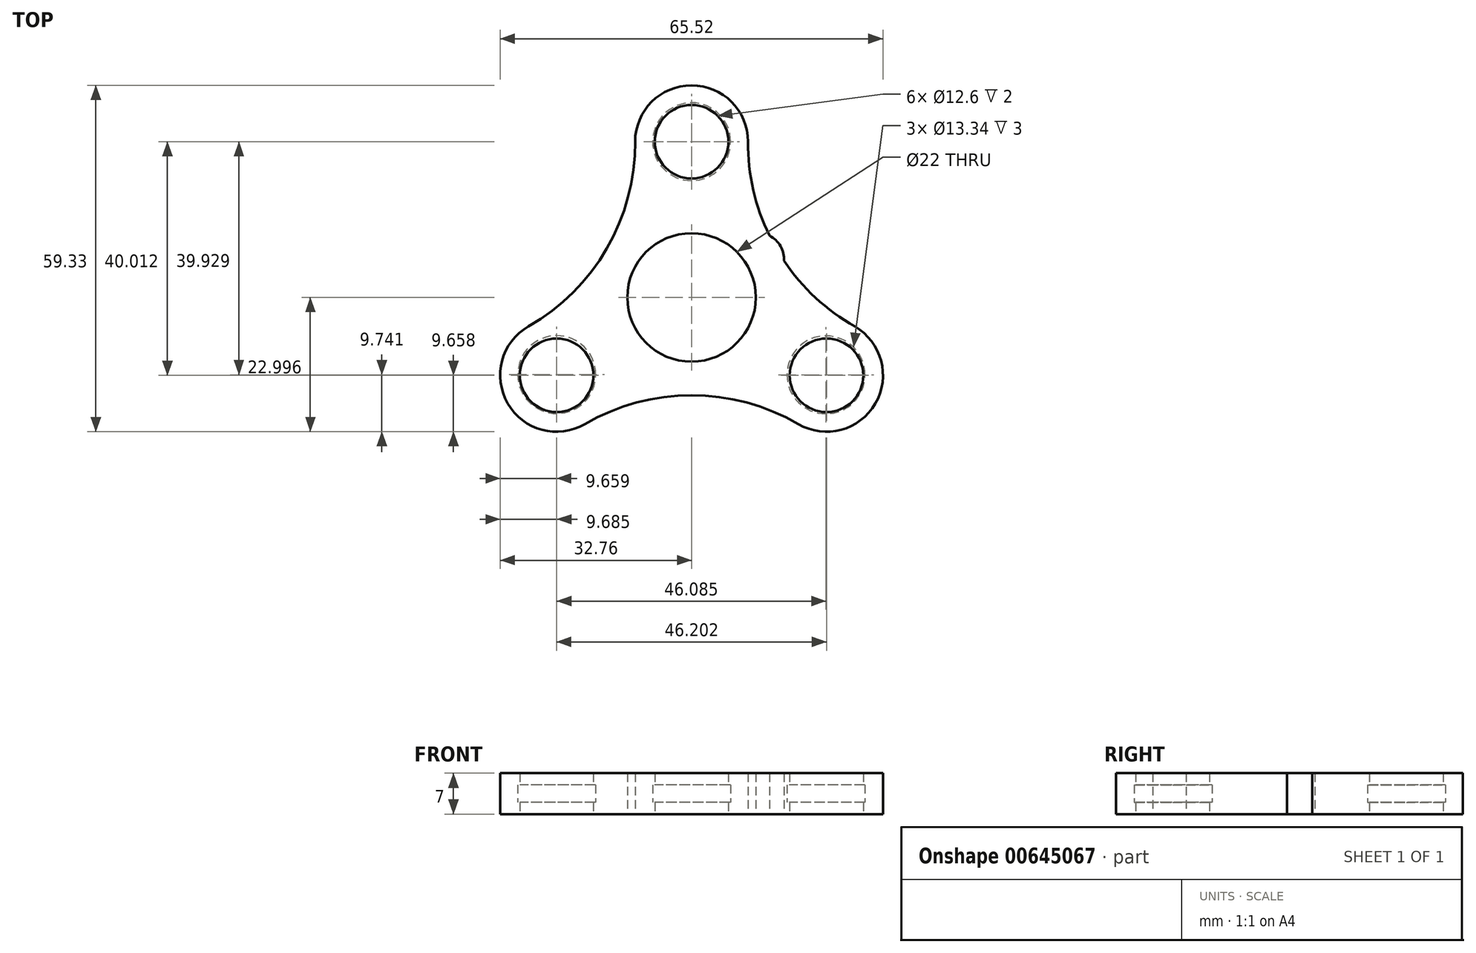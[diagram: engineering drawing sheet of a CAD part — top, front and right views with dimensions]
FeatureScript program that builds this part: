
annotation { "Feature Type Name" : "Feature", "Feature Type Description" : "" }
export const myFeature = defineFeature(function(context is Context, id is Id, definition is map)
    precondition{}
    {
        {
            var Q0;
            Q0=qCreatedBy(makeId("Top.planeOp"),FACE);
            var sketch = newSketch(context, id + "F0", { "sketchPlane" : qUnion([Q0])});
            skCircle(sketch, "E0", {"center": v(0, 0) * mm, "radius": 6.3 * mm});
            skCircle(sketch, "E1", {"center": v(0, 0) * mm, "radius": 9.66 * mm});
            skCircle(sketch, "E2.1.0", {"center": v(-23.1, -40.01) * mm, "radius": 9.66 * mm});
            skCircle(sketch, "E2.1.1", {"center": v(-23.1, -40.01) * mm, "radius": 6.3 * mm});
            skCircle(sketch, "E2.2.0", {"center": v(23.1, -40.01) * mm, "radius": 9.66 * mm});
            skCircle(sketch, "E2.2.1", {"center": v(23.1, -40.01) * mm, "radius": 6.3 * mm});
            skPoint(sketch, "E2.center", {"position": v(0, -26.67) * mm});
            skLineSegment(sketch, "E3", {"start": v(0, 0) * mm, "end": v(-9.66, 0) * mm, "construction": true});
            skCircle(sketch, "E4", {"center": v(0, -26.67) * mm, "radius": 11 * mm});
            skLineSegment(sketch, "E5", {"start": v(0, -26.67) * mm, "end": v(-23.1, -40.01) * mm, "construction": true});
            skLineSegment(sketch, "E6", {"start": v(23.1, -40.01) * mm, "end": v(0, -26.67) * mm, "construction": true});
            skLineSegment(sketch, "E7", {"start": v(0, -26.67) * mm, "end": v(0, 0) * mm, "construction": true});
            skLineSegment(sketch, "E8", {"start": v(23.1, -40.01) * mm, "end": v(27.93, -31.64) * mm, "construction": true});
            skLineSegment(sketch, "E9", {"start": v(0, 0) * mm, "end": v(9.66, 0) * mm, "construction": true});
            skLineSegment(sketch, "E10", {"start": v(-23.1, -40.01) * mm, "end": v(-27.93, -31.64) * mm, "construction": true});
            skArc(sketch, "E11", {"start": v(-27.93, -31.64) * mm, "mid": v(-14.5, -18.3) * mm, "end": v(-9.66, 0) * mm});
            skArc(sketch, "E12", {"start": v(9.66, 0) * mm, "mid": v(14.5, -18.3) * mm, "end": v(27.93, -31.64) * mm});
            skLineSegment(sketch, "E13", {"start": v(-23.1, -40.01) * mm, "end": v(-18.27, -48.38) * mm, "construction": true});
            skLineSegment(sketch, "E14", {"start": v(23.1, -40.01) * mm, "end": v(18.27, -48.38) * mm, "construction": true});
            skArc(sketch, "E15", {"start": v(18.27, -48.38) * mm, "mid": v(0, -43.43) * mm, "end": v(-18.27, -48.38) * mm});
            skLineSegment(sketch, "E16", {"start": v(0, -26.67) * mm, "end": v(-14.5, -18.3) * mm, "construction": true});
            skLineSegment(sketch, "E17", {"start": v(-14.5, -18.3) * mm, "end": v(0, -26.67) * mm, "construction": true});
            skLineSegment(sketch, "E18", {"start": v(0, -26.67) * mm, "end": v(14.5, -18.3) * mm, "construction": true});
            skLineSegment(sketch, "E19", {"start": v(0, -26.67) * mm, "end": v(0, -43.43) * mm, "construction": true});
            skLineSegment(sketch, "E20", {"start": v(14.5, -18.3) * mm, "end": v(15.83, -20.42) * mm, "construction": true});
            skLineSegment(sketch, "E21", {"start": v(14.5, -18.3) * mm, "end": v(13.33, -16.1) * mm, "construction": true});
            skArc(sketch, "E22", {"start": v(15.83, -20.42) * mm, "mid": v(15.22, -17.89) * mm, "end": v(13.33, -16.1) * mm});
            skArc(sketch, "E23.MirrorCS", {"start": v(-15.83, -20.42) * mm, "mid": v(-15.22, -17.89) * mm, "end": v(-13.33, -16.1) * mm});
            skArc(sketch, "E24.MirrorCS", {"start": v(2.5, -43.51) * mm, "mid": v(0, -44.25) * mm, "end": v(-2.5, -43.51) * mm});
            skSolve(sketch);
        }
        {
            var Q0;
            Q0=makeQuery(id+"F0.imprint","IMPRINT",FACE,{"disambiguationData":[TD([[makeQuery(id+"F0.imprint","IMPRINT",EDGE,{"derivedFrom":sQuery(id+"F0.wireOp",EDGE,"E0")}),-1.0]])]});
            var Q1;
            Q1=makeQuery(id+"F0.imprint","IMPRINT",FACE,{"disambiguationData":[TD([[makeQuery(id+"F0.imprint","IMPRINT",EDGE,{"derivedFrom":sQuery(id+"F0.wireOp",EDGE,"E2.1.1")}),-1.0]])]});
            var Q2;
            Q2=makeQuery(id+"F0.imprint","IMPRINT",FACE,{"disambiguationData":[TD([[makeQuery(id+"F0.imprint","IMPRINT",EDGE,{"derivedFrom":sQuery(id+"F0.wireOp",EDGE,"E2.2.1")}),-1.0]])]});
            var Q3;
            {var subQ0=sQuery(id+"F0.wireOp",EDGE,"UzU74dU8-enYz-kkmd-C7oZ-pswxIBgTCVmV");var subQ1=sQuery(id+"F0.wireOp",EDGE,"E12");var subQ2=makeQuery(id+"F0.imprint","INTERSECT",VERTEX,{"disambiguationData":[OD(1.0)],"derivedFrom":[subQ1,subQ0]});Q3=makeQuery(id+"F0.imprint","IMPRINT",FACE,{"disambiguationData":[TD([[makeQuery(id+"F0.imprint","IMPRINT",EDGE,{"disambiguationData":[TD([[subQ2,-1.0]])],"derivedFrom":subQ1}),1.0]])]});}
            var Q4;
            {var subQ0=sQuery(id+"F0.wireOp",EDGE,"d11itaW9-BDd3-fUXO-ILgY-40LG9F4n92Nl");var subQ1=sQuery(id+"F0.wireOp",EDGE,"E12");var subQ2=makeQuery(id+"F0.imprint","INTERSECT",VERTEX,{"disambiguationData":[OD(1.0)],"derivedFrom":[subQ1,subQ0]});Q4=makeQuery(id+"F0.imprint","IMPRINT",FACE,{"disambiguationData":[TD([[makeQuery(id+"F0.imprint","IMPRINT",EDGE,{"disambiguationData":[TD([[subQ2,-1.0]])],"derivedFrom":subQ1}),1.0]])]});}
            var Q5;
            Q5=makeQuery(id+"F0.imprint","IMPRINT",FACE,{"disambiguationData":[TD([[makeQuery(id+"F0.imprint","IMPRINT",EDGE,{"derivedFrom":sQuery(id+"F0.wireOp",EDGE,"E4")}),-1.0]])]});
            var Q6;
            {var subQ0=sQuery(id+"F0.wireOp",EDGE,"E22");Q6=makeQuery(id+"F0.imprint","IMPRINT",FACE,{"disambiguationData":[TD([[makeQuery(id+"F0.imprint","IMPRINT",EDGE,{"derivedFrom":subQ0}),1.0]])]});}
            var Q7;
            {var subQ0=sQuery(id+"F0.wireOp",EDGE,"E23.MirrorCS");Q7=makeQuery(id+"F0.imprint","IMPRINT",FACE,{"disambiguationData":[TD([[makeQuery(id+"F0.imprint","IMPRINT",EDGE,{"derivedFrom":subQ0}),-1.0]])]});}
            var Q8;
            {var subQ0=sQuery(id+"F0.wireOp",EDGE,"E24.MirrorCS");Q8=makeQuery(id+"F0.imprint","IMPRINT",FACE,{"disambiguationData":[TD([[makeQuery(id+"F0.imprint","IMPRINT",EDGE,{"derivedFrom":subQ0}),-1.0]])]});}
            extrude(context, id + "F1", {"entities" : qUnion([Q0, Q1, Q2, Q3, Q4, Q5, Q6, Q7, Q8]), "depth" : 7 * mm, "offsetDistance" : 25 * mm});
        }
        {
            var Q0;
            Q0=qCreatedBy(makeId("Right.planeOp"),FACE);
            var sketch = newSketch(context, id + "F2", { "sketchPlane" : qUnion([Q0])});
            skLineSegment(sketch, "E25", {"start": v(18.83, 0) * mm, "end": v(18.83, 4) * mm, "construction": true});
            skSolve(sketch);
        }
        {
            var Q0;
            Q0=sQuery(id+"F2.wireOp",EDGE,"E25");
            cPlane(context, id + "F3", {"entities" : qUnion([Q0]), "cplaneType" : CPlaneType.MID_PLANE, "offset" : 25 * mm, "width" : 150 * mm, "height" : 150 * mm});
        }
        {
            var Q0;
            Q0=qCreatedBy(id+"F3.planeOp",FACE);
            var sketch = newSketch(context, id + "F4", { "sketchPlane" : qUnion([Q0])});
            skCircle(sketch, "E26", {"center": v(0, 0) * mm, "radius": 6.67 * mm});
            skCircle(sketch, "E27.1.0", {"center": v(-23.07, -39.9) * mm, "radius": 6.67 * mm});
            skCircle(sketch, "E27.2.0", {"center": v(23.01, -39.93) * mm, "radius": 6.67 * mm});
            skPoint(sketch, "E27.center", {"position": v(-0.02, -26.6) * mm});
            skSolve(sketch);
        }
        {
            var Q0;
            Q0=qSketchRegion(id+"F4",true);
            extrude(context, id + "F5", {"entities" : qUnion([Q0]), "operationType" : NewBodyOperationType.REMOVE, "depth" : 3 * mm, "offsetDistance" : 25 * mm});
        }
    });
